# Revit family: 3.Электрический нагреватель для круглых каналов ELK
name_source: partatom
category: Оборудование
revit_build: Autodesk Revit 2016 (Build: 20151209_0715(x64)
units: mm (PartAtom-declared; Revit-internal decimal feet)

## family parameters
Всегда вертикально = Да
На основе рабочей плоскости = Нет
Общий = Нет
При загрузке вырезать с полостями = Нет
Размер круглого соединителя = Использовать диаметр
Тип детали = Нормальный
Точка расчета площади = Нет

## types (25) — shared parameters
Единица измерения = шт.
Завод изготовитель = KORF
Заправочный объем, л = 0.4 м³
Ключевая пометка = Вентиляция
Материал = Сталь серая
Наименование и тех.хар-ка = Электрический нагреватель для круглых каналов
Раздел = ОВ
отступ = 30 мм

## per-type parameters (varying)
| type | B | R | А | Б | Г | Д | Д1 | Масса единицы | Мощность, кВт | Напряжение U,В | Сила тока J, А | Силовой кабель | Тип, марка, обозначение |
| 100/0,5 | 100 мм | 52 мм | 271 мм | 297 мм | 74 мм | 104 мм | 98 мм | 1,4 кг | 1 Вт | 1-220 | 2.27 | ВВГ 3х1,5/1 | ELK 100/0.5 |
| 100/1.5 | 100 мм | 52 мм | 271 мм | 360 мм | 74 мм | 104 мм | 98 мм | 1,8 кг | 2 Вт | 1-220 | 6.8 | ВВГ 3х1,5/1 | ELK 100/1.5 |
| 100/2 | 100 мм | 52 мм | 346 мм | 410 мм | 74 мм | 104 мм | 98 мм | 2.2 кг | 2 Вт | 1-220 | 9.1 | ВВГ 3х2,5/1 | ELK 100/2 |
| 100/2.5 | 100 мм | 52 мм | 346 мм | 455 мм | 74 мм | 104 мм | 98 мм | 2.4 кг | 3 Вт | 1-220 | 11.3 | ВВГ 3х2,5/1 | ELK 100/2.5 |
| 125/1.5 | 125 мм | 65 мм | 271 мм | 330 мм | 82 мм | 129 мм | 123 мм | 1.9 кг | 2 Вт | 1-220 | 6.8 | ВВГ 3х1,5/1 | ELK 125/1.5 |
| 125/2 | 125 мм | 65 мм | 271 мм | 330 мм | 82 мм | 129 мм | 123 мм | 2 кг | 2 Вт | 1-220 | 9.1 | ВВГ 3х2,5/1 | ELK 125/2 |
| 125/2.5 | 125 мм | 65 мм | 271 мм | 347 мм | 82 мм | 129 мм | 123 мм | 2.3 кг | 3 Вт | 1-220 | 11.3 | ВВГ 3х2,5/1 | ELK 125/2.5 |
| 125/3 | 125 мм | 65 мм | 271 мм | 347 мм | 82 мм | 129 мм | 123 мм | 2.4 кг | 3 Вт | 1-220 | 13.6 | ВВГ 3х2,5/1 | ELK 125/3 |
| 160/2 | 160 мм | 82 мм | 271 мм | 370 мм | 83 мм | 164 мм | 157 мм | 2.6 кг | 2 Вт | 1-220 | 9.1 | ВВГ 3х2,5/1 | ELK 160/2 |
| 160/3 | 160 мм | 82 мм | 271 мм | 370 мм | 83 мм | 164 мм | 157 мм | 2.8 кг | 3 Вт | 1-220 | 13.6 | ВВГ 3х2,5/1 | ELK 160/3 |
| 160/4.5 | 160 мм | 82 мм | 271 мм | 370 мм | 83 мм | 164 мм | 157 мм | 3.2 кг | 5 Вт | 3-380 | 6.8 | ВВГ 4х2,5/1 | ELK 160/4.5 |
| 160/6 | 160 мм | 82 мм | 391 мм | 490 мм | 83 мм | 164 мм | 157 мм | 4.2 кг | 6 Вт | 3-380 | 9.1 | ВВГ 4х2,5/1 | ELK 160/6 |
| 200/3 | 200 мм | 102 мм | 271 мм | 370 мм | 86 мм | 204 мм | 196 мм | 3.2 кг | 3 Вт | 1-220 | 13.6 | ВВГ 3х2,5/1 | ELK 200/3 |
| 200/6 | 200 мм | 102 мм | 271 мм | 370 мм | 86 мм | 204 мм | 196 мм | 4 кг | 6 Вт | 3-380 | 9.1 | ВВГ 4х2,5/1 | ELK 200/6 |
| 200/9 | 200 мм | 102 мм | 391 мм | 490 мм | 86 мм | 204 мм | 196 мм | 5.2 кг | 9 Вт | 3-380 | 13.6 | ВВГ 4х2,5/1 | ELK 200/9 |
| 200/12 | 200 мм | 102 мм | 391 мм | 490 мм | 86 мм | 204 мм | 196 мм | 6.2 кг | 12 Вт | 3-380 | 18.1 | ВВГ 4х2,5/2 | ELK 200/12 |
| 250/6 | 250 мм | 127 мм | 271 мм | 370 мм | 99 мм | 254 мм | 245 мм | 5.6 кг | 6 Вт | 3-380 | 9.1 | ВВГ 4х2,5/1 | ELK 250/6 |
| 250/9 | 250 мм | 127 мм | 271 мм | 370 мм | 99 мм | 254 мм | 245 мм | 6 кг | 9 Вт | 3-380 | 13.6 | ВВГ 4х2,5/1 | ELK 250/6 |
| 250/12 | 250 мм | 127 мм | 391 мм | 490 мм | 99 мм | 254 мм | 245 мм | 8.6 кг | 12 Вт | 3-380 | 19.1 | ВВГ 4х2,5/2 | ELK 250/12 |
| 250/15 | 250 мм | 127 мм | 391 мм | 490 мм | 99 мм | 254 мм | 245 мм | 8.65 кг | 15 Вт | 3-380 | 22.7 | ВВГ 4х2,5/2 | ELK 250/15 |
| 315/6 | 315 мм | 160 мм | 271 мм | 370 мм | 98 мм | 319 мм | 309 мм | 6.6 кг | 6 Вт | 3-380 | 9.1 | ВВГ 4х2,5/1 | ELK 315/6 |
| 315/9 | 315 мм | 160 мм | 271 мм | 370 мм | 98 мм | 319 мм | 309 мм | 6.8 кг | 9 Вт | 3-380 | 13.6 | ВВГ 4х2,5/1 | ELK 315/9 |
| 315/12 | 315 мм | 160 мм | 391 мм | 490 мм | 98 мм | 319 мм | 309 мм | 9.6 кг | 12 Вт | 3-380 | 18.1 | ВВГ 4х2,5/2 | ELK 315/12 |
| 315/15 | 315 мм | 160 мм | 391 мм | 490 мм | 98 мм | 319 мм | 309 мм | 9.65 кг | 15 Вт | 3-380 | 22.7 | ВВГ 4х2,5/2 | ELK 315/15 |
| 315/18 | 315 мм | 160 мм | 391 мм | 490 мм | 98 мм | 319 мм | 309 мм | 10.4 кг | 18 Вт | 3-380 | 27.2 | ВВГ 4х2,5/2 | ELK 315/18 |
